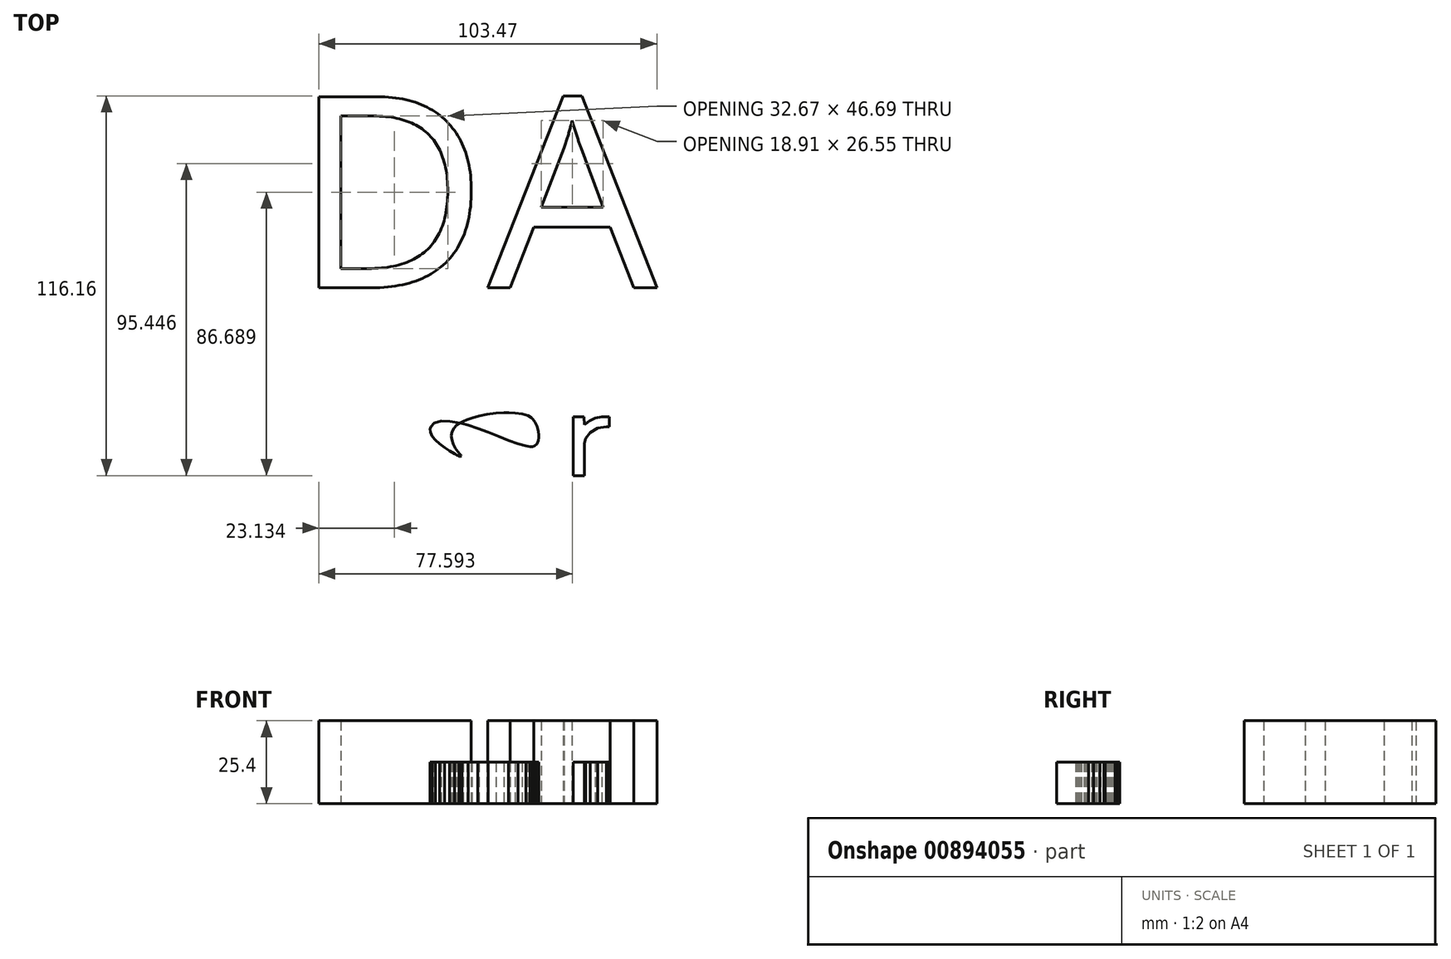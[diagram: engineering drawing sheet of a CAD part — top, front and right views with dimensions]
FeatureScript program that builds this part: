
annotation { "Feature Type Name" : "Feature", "Feature Type Description" : "" }
export const myFeature = defineFeature(function(context is Context, id is Id, definition is map)
    precondition{}
    {
        {
            var Q0;
            Q0=qCreatedBy(makeId("Top.planeOp"),FACE);
            var sketch = newSketch(context, id + "F0", { "sketchPlane" : qUnion([Q0])});
            skLineSegment(sketch, "E0", {"start": v(38.55, 8.55) * mm, "end": v(38.55, 11.6) * mm});
            skLineSegment(sketch, "E1", {"start": v(38.55, 11.6) * mm, "end": v(37.96, 11.65) * mm});
            skLineSegment(sketch, "E2", {"start": v(37.96, 11.65) * mm, "end": v(36.18, 11.62) * mm});
            skLineSegment(sketch, "E3", {"start": v(36.18, 11.62) * mm, "end": v(34.15, 11.22) * mm});
            skLineSegment(sketch, "E4", {"start": v(34.15, 11.22) * mm, "end": v(32.41, 10.4) * mm});
            skLineSegment(sketch, "E5", {"start": v(32.41, 10.4) * mm, "end": v(31.25, 9.5) * mm});
            skLineSegment(sketch, "E6", {"start": v(31.25, 9.5) * mm, "end": v(30.91, 9.15) * mm});
            skLineSegment(sketch, "E7", {"start": v(30.91, 9.15) * mm, "end": v(30.73, 11.63) * mm});
            skLineSegment(sketch, "E8", {"start": v(30.73, 11.63) * mm, "end": v(27.47, 11.63) * mm});
            skLineSegment(sketch, "E9", {"start": v(27.47, 11.63) * mm, "end": v(27.47, -6.37) * mm});
            skLineSegment(sketch, "E10", {"start": v(27.47, -6.37) * mm, "end": v(30.91, -6.37) * mm});
            skLineSegment(sketch, "E11", {"start": v(30.91, -6.37) * mm, "end": v(30.91, 2.96) * mm});
            skLineSegment(sketch, "E12", {"start": v(30.91, 2.96) * mm, "end": v(30.91, 3.46) * mm});
            skLineSegment(sketch, "E13", {"start": v(30.91, 3.46) * mm, "end": v(31.33, 4.97) * mm});
            skLineSegment(sketch, "E14", {"start": v(31.33, 4.97) * mm, "end": v(32.65, 6.85) * mm});
            skLineSegment(sketch, "E15", {"start": v(32.65, 6.85) * mm, "end": v(35.02, 8.17) * mm});
            skLineSegment(sketch, "E16", {"start": v(35.02, 8.17) * mm, "end": v(37.67, 8.6) * mm});
            skLineSegment(sketch, "E17", {"start": v(37.67, 8.6) * mm, "end": v(38.55, 8.55) * mm});
            skLineSegment(sketch, "E18", {"start": v(-7.86, 9.23) * mm, "end": v(-7.81, 9.26) * mm});
            skLineSegment(sketch, "E19", {"start": v(-7.81, 9.26) * mm, "end": v(-7.28, 9.6) * mm});
            skLineSegment(sketch, "E20", {"start": v(-7.28, 9.6) * mm, "end": v(-7.23, 9.62) * mm});
            skLineSegment(sketch, "E21", {"start": v(-7.23, 9.62) * mm, "end": v(-7.16, 9.66) * mm});
            skLineSegment(sketch, "E22", {"start": v(-7.16, 9.66) * mm, "end": v(-7.23, 9.67) * mm});
            skLineSegment(sketch, "E23", {"start": v(-7.23, 9.67) * mm, "end": v(-7.97, 9.87) * mm});
            skLineSegment(sketch, "E24", {"start": v(-7.97, 9.87) * mm, "end": v(-10.25, 10.27) * mm});
            skLineSegment(sketch, "E25", {"start": v(-10.25, 10.27) * mm, "end": v(-12.96, 10.31) * mm});
            skLineSegment(sketch, "E26", {"start": v(-12.96, 10.31) * mm, "end": v(-15.04, 9.66) * mm});
            skLineSegment(sketch, "E27", {"start": v(-15.04, 9.66) * mm, "end": v(-16.06, 8.6) * mm});
            skLineSegment(sketch, "E28", {"start": v(-16.06, 8.6) * mm, "end": v(-16.19, 8.19) * mm});
            skLineSegment(sketch, "E29", {"start": v(-16.19, 8.19) * mm, "end": v(-16.28, 7.9) * mm});
            skLineSegment(sketch, "E30", {"start": v(-16.28, 7.9) * mm, "end": v(-16.24, 6.94) * mm});
            skLineSegment(sketch, "E31", {"start": v(-16.24, 6.94) * mm, "end": v(-15.7, 5.7) * mm});
            skLineSegment(sketch, "E32", {"start": v(-15.7, 5.7) * mm, "end": v(-14.72, 4.47) * mm});
            skLineSegment(sketch, "E33", {"start": v(-14.72, 4.47) * mm, "end": v(-13.42, 3.3) * mm});
            skLineSegment(sketch, "E34", {"start": v(-13.42, 3.3) * mm, "end": v(-11.92, 2.21) * mm});
            skLineSegment(sketch, "E35", {"start": v(-11.92, 2.21) * mm, "end": v(-10.36, 1.22) * mm});
            skLineSegment(sketch, "E36", {"start": v(-10.36, 1.22) * mm, "end": v(-8.87, 0.35) * mm});
            skLineSegment(sketch, "E37", {"start": v(-8.87, 0.35) * mm, "end": v(-7.9, -0.19) * mm});
            skLineSegment(sketch, "E38", {"start": v(-7.9, -0.19) * mm, "end": v(-7.57, -0.37) * mm});
            skLineSegment(sketch, "E39", {"start": v(-7.57, -0.37) * mm, "end": v(-7.48, -0.42) * mm});
            skLineSegment(sketch, "E40", {"start": v(-7.48, -0.42) * mm, "end": v(-7.15, -0.53) * mm});
            skLineSegment(sketch, "E41", {"start": v(-7.15, -0.53) * mm, "end": v(-6.9, -0.5) * mm});
            skLineSegment(sketch, "E42", {"start": v(-6.9, -0.5) * mm, "end": v(-6.86, -0.33) * mm});
            skLineSegment(sketch, "E43", {"start": v(-6.86, -0.33) * mm, "end": v(-6.99, -0.08) * mm});
            skLineSegment(sketch, "E44", {"start": v(-6.99, -0.08) * mm, "end": v(-7.05, -0.02) * mm});
            skLineSegment(sketch, "E45", {"start": v(-7.05, -0.02) * mm, "end": v(-7.24, 0.21) * mm});
            skLineSegment(sketch, "E46", {"start": v(-7.24, 0.21) * mm, "end": v(-7.8, 0.92) * mm});
            skLineSegment(sketch, "E47", {"start": v(-7.8, 0.92) * mm, "end": v(-8.55, 2.01) * mm});
            skLineSegment(sketch, "E48", {"start": v(-8.55, 2.01) * mm, "end": v(-9.2, 3.21) * mm});
            skLineSegment(sketch, "E49", {"start": v(-9.2, 3.21) * mm, "end": v(-9.65, 4.48) * mm});
            skLineSegment(sketch, "E50", {"start": v(-9.65, 4.48) * mm, "end": v(-9.84, 5.76) * mm});
            skLineSegment(sketch, "E51", {"start": v(-9.84, 5.76) * mm, "end": v(-9.66, 7) * mm});
            skLineSegment(sketch, "E52", {"start": v(-9.66, 7) * mm, "end": v(-9.03, 8.18) * mm});
            skLineSegment(sketch, "E53", {"start": v(-9.03, 8.18) * mm, "end": v(-8.18, 9.02) * mm});
            skLineSegment(sketch, "E54", {"start": v(-8.18, 9.02) * mm, "end": v(-7.86, 9.23) * mm});
            skLineSegment(sketch, "E55", {"start": v(-7.17, 9.66) * mm, "end": v(-6.93, 9.8) * mm});
            skLineSegment(sketch, "E56", {"start": v(-6.93, 9.8) * mm, "end": v(-6.22, 10.17) * mm});
            skLineSegment(sketch, "E57", {"start": v(-6.22, 10.17) * mm, "end": v(-5.05, 10.69) * mm});
            skLineSegment(sketch, "E58", {"start": v(-5.05, 10.69) * mm, "end": v(-3.44, 11.28) * mm});
            skLineSegment(sketch, "E59", {"start": v(-3.44, 11.28) * mm, "end": v(-1.4, 11.88) * mm});
            skLineSegment(sketch, "E60", {"start": v(-1.4, 11.88) * mm, "end": v(1.05, 12.4) * mm});
            skLineSegment(sketch, "E61", {"start": v(1.05, 12.4) * mm, "end": v(3.9, 12.77) * mm});
            skLineSegment(sketch, "E62", {"start": v(3.9, 12.77) * mm, "end": v(6.33, 12.91) * mm});
            skLineSegment(sketch, "E63", {"start": v(6.33, 12.91) * mm, "end": v(7.14, 12.91) * mm});
            skLineSegment(sketch, "E64", {"start": v(7.14, 12.91) * mm, "end": v(7.77, 12.91) * mm});
            skLineSegment(sketch, "E65", {"start": v(7.77, 12.91) * mm, "end": v(9.67, 12.8) * mm});
            skLineSegment(sketch, "E66", {"start": v(9.67, 12.8) * mm, "end": v(11.88, 12.49) * mm});
            skLineSegment(sketch, "E67", {"start": v(11.88, 12.49) * mm, "end": v(13.67, 11.93) * mm});
            skLineSegment(sketch, "E68", {"start": v(13.67, 11.93) * mm, "end": v(14.66, 11.38) * mm});
            skLineSegment(sketch, "E69", {"start": v(14.66, 11.38) * mm, "end": v(14.92, 11.13) * mm});
            skLineSegment(sketch, "E70", {"start": v(14.92, 11.13) * mm, "end": v(15.17, 10.88) * mm});
            skLineSegment(sketch, "E71", {"start": v(15.17, 10.88) * mm, "end": v(15.8, 10) * mm});
            skLineSegment(sketch, "E72", {"start": v(15.8, 10) * mm, "end": v(16.44, 8.64) * mm});
            skLineSegment(sketch, "E73", {"start": v(16.44, 8.64) * mm, "end": v(16.83, 7.14) * mm});
            skLineSegment(sketch, "E74", {"start": v(16.83, 7.14) * mm, "end": v(16.96, 5.99) * mm});
            skLineSegment(sketch, "E75", {"start": v(16.96, 5.99) * mm, "end": v(16.96, 5.6) * mm});
            skLineSegment(sketch, "E76", {"start": v(16.96, 5.6) * mm, "end": v(16.96, 5.3) * mm});
            skLineSegment(sketch, "E77", {"start": v(16.96, 5.3) * mm, "end": v(16.83, 4.38) * mm});
            skLineSegment(sketch, "E78", {"start": v(16.83, 4.38) * mm, "end": v(16.42, 3.36) * mm});
            skLineSegment(sketch, "E79", {"start": v(16.42, 3.36) * mm, "end": v(15.72, 2.67) * mm});
            skLineSegment(sketch, "E80", {"start": v(15.72, 2.67) * mm, "end": v(14.99, 2.42) * mm});
            skLineSegment(sketch, "E81", {"start": v(14.99, 2.42) * mm, "end": v(14.74, 2.42) * mm});
            skLineSegment(sketch, "E82", {"start": v(14.74, 2.42) * mm, "end": v(14.3, 2.42) * mm});
            skLineSegment(sketch, "E83", {"start": v(14.3, 2.42) * mm, "end": v(12.95, 2.68) * mm});
            skLineSegment(sketch, "E84", {"start": v(12.95, 2.68) * mm, "end": v(10.55, 3.39) * mm});
            skLineSegment(sketch, "E85", {"start": v(10.55, 3.39) * mm, "end": v(7.72, 4.4) * mm});
            skLineSegment(sketch, "E86", {"start": v(7.72, 4.4) * mm, "end": v(4.62, 5.6) * mm});
            skLineSegment(sketch, "E87", {"start": v(4.62, 5.6) * mm, "end": v(1.41, 6.87) * mm});
            skLineSegment(sketch, "E88", {"start": v(1.41, 6.87) * mm, "end": v(-1.73, 8.05) * mm});
            skLineSegment(sketch, "E89", {"start": v(-1.73, 8.05) * mm, "end": v(-4.64, 9.02) * mm});
            skLineSegment(sketch, "E90", {"start": v(-4.64, 9.02) * mm, "end": v(-6.53, 9.54) * mm});
            skLineSegment(sketch, "E91", {"start": v(-6.53, 9.54) * mm, "end": v(-7.17, 9.66) * mm});
            skSolve(sketch);
        }
        {
            var Q0;
            {var subQ5=sQuery(id+"F0.wireOp",EDGE,"E56");Q0=makeQuery(id+"F0.imprint","IMPRINT",FACE,{"disambiguationData":[TD([[makeQuery(id+"F0.imprint","IMPRINT",EDGE,{"derivedFrom":subQ5}),-1.0]])]});}
            var Q1;
            Q1=makeQuery(id+"F0.imprint","IMPRINT",FACE,{"disambiguationData":[TD([[makeQuery(id+"F0.imprint","IMPRINT",EDGE,{"derivedFrom":sQuery(id+"F0.wireOp",EDGE,"1403de3f-786f-42e8-bdc0-92bf3ea4d2cf")}),-1.0]])]});
            var Q2;
            Q2=makeQuery(id+"F0.imprint","IMPRINT",FACE,{"disambiguationData":[TD([[makeQuery(id+"F0.imprint","IMPRINT",EDGE,{"derivedFrom":sQuery(id+"F0.wireOp",EDGE,"95009ed1-91f1-4808-89fd-04971f9fd36b")}),-1.0]])]});
            var Q3;
            Q3=makeQuery(id+"F0.imprint","IMPRINT",FACE,{"disambiguationData":[TD([[makeQuery(id+"F0.imprint","IMPRINT",EDGE,{"derivedFrom":sQuery(id+"F0.wireOp",EDGE,"E0")}),1.0]])]});
            var Q4;
            Q4=makeQuery(id+"F0.imprint","IMPRINT",FACE,{"disambiguationData":[TD([[makeQuery(id+"F0.imprint","IMPRINT",EDGE,{"derivedFrom":sQuery(id+"F0.wireOp",EDGE,"537d8619-0df1-4f76-a38b-5c3195fe6c56")}),1.0]])]});
            var Q5;
            Q5=makeQuery(id+"F0.imprint","IMPRINT",FACE,{"disambiguationData":[TD([[makeQuery(id+"F0.imprint","IMPRINT",EDGE,{"derivedFrom":sQuery(id+"F0.wireOp",EDGE,"53540bf8-cc36-49fe-be7e-849ee8bb7355")}),-1.0]])]});
            var Q6;
            Q6=makeQuery(id+"F0.imprint","IMPRINT",FACE,{"disambiguationData":[TD([[makeQuery(id+"F0.imprint","IMPRINT",EDGE,{"derivedFrom":sQuery(id+"F0.wireOp",EDGE,"5d299cd5-eb9d-4ea7-a19f-d956b55c55ad")}),-1.0]])]});
            var Q7;
            Q7=makeQuery(id+"F0.imprint","IMPRINT",FACE,{"disambiguationData":[TD([[makeQuery(id+"F0.imprint","IMPRINT",EDGE,{"derivedFrom":sQuery(id+"F0.wireOp",EDGE,"88f4a6f8-3216-4552-9583-ee77e8b5c767")}),-1.0]])]});
            var Q8;
            {var subQ0=sQuery(id+"F0.wireOp",EDGE,"499cde78-be49-40a4-880d-d042f24b3584");Q8=makeQuery(id+"F0.imprint","IMPRINT",FACE,{"disambiguationData":[TD([[makeQuery(id+"F0.imprint","IMPRINT",EDGE,{"derivedFrom":subQ0}),-1.0]])]});}
            var Q9;
            Q9=makeQuery(id+"F0.imprint","IMPRINT",FACE,{"disambiguationData":[TD([[makeQuery(id+"F0.imprint","IMPRINT",EDGE,{"derivedFrom":sQuery(id+"F0.wireOp",EDGE,"f5d51b6b-fd86-4680-a26f-6e4a6e33f496")}),-1.0]])]});
            var Q10;
            Q10=makeQuery(id+"F0.imprint","IMPRINT",FACE,{"disambiguationData":[TD([[makeQuery(id+"F0.imprint","IMPRINT",EDGE,{"derivedFrom":sQuery(id+"F0.wireOp",EDGE,"E18")}),1.0]])]});
            var Q11;
            Q11=makeQuery(id+"F0.imprint","IMPRINT",FACE,{"disambiguationData":[TD([[makeQuery(id+"F0.imprint","IMPRINT",EDGE,{"derivedFrom":sQuery(id+"F0.wireOp",EDGE,"d14cbd88-a913-48c0-9fde-35ce2438bb89")}),1.0]])]});
            var Q12;
            Q12=makeQuery(id+"F0.imprint","IMPRINT",FACE,{"disambiguationData":[TD([[makeQuery(id+"F0.imprint","IMPRINT",EDGE,{"derivedFrom":sQuery(id+"F0.wireOp",EDGE,"56bfb7e6-9a1f-421a-9683-003b9129566a")}),1.0]])]});
            var Q13;
            Q13=makeQuery(id+"F0.imprint","IMPRINT",FACE,{"disambiguationData":[TD([[makeQuery(id+"F0.imprint","IMPRINT",EDGE,{"derivedFrom":sQuery(id+"F0.wireOp",EDGE,"ad045c7c-f0ab-4b8a-855a-bf2486b68ccc")}),1.0]])]});
            var Q14;
            Q14=makeQuery(id+"F0.imprint","IMPRINT",FACE,{"disambiguationData":[TD([[makeQuery(id+"F0.imprint","IMPRINT",EDGE,{"derivedFrom":sQuery(id+"F0.wireOp",EDGE,"f15a1d2e-a023-4afb-ae37-dc3aa092487f")}),1.0]])]});
            var Q15;
            {var subQ0=sQuery(id+"F0.wireOp",EDGE,"907b8c1e-9dad-4756-b5b3-93d8dea9a1bf");var subQ1=sQuery(id+"F0.wireOp",EDGE,"2761c65c-d06f-425f-8b3a-7dbb7bd44bb6");var subQ2=makeQuery(id+"F0.imprint","INTERSECT",VERTEX,{"derivedFrom":[subQ1,subQ0]});Q15=makeQuery(id+"F0.imprint","IMPRINT",FACE,{"disambiguationData":[TD([[makeQuery(id+"F0.imprint","IMPRINT",EDGE,{"disambiguationData":[TD([[subQ2,1.0]])],"derivedFrom":subQ1}),1.0]])]});}
            var Q16;
            {var subQ0=sQuery(id+"F0.wireOp",EDGE,"E22");var subQ1=sQuery(id+"F0.wireOp",EDGE,"E21");var subQ2=makeQuery(id+"F0.imprint","INTERSECT",VERTEX,{"derivedFrom":[subQ1,subQ0]});Q16=makeQuery(id+"F0.imprint","IMPRINT",FACE,{"disambiguationData":[TD([[makeQuery(id+"F0.imprint","IMPRINT",EDGE,{"disambiguationData":[TD([[subQ2,1.0]])],"derivedFrom":subQ1}),1.0]])]});}
            var Q17;
            Q17=makeQuery(id+"F0.imprint","IMPRINT",FACE,{"disambiguationData":[TD([[makeQuery(id+"F0.imprint","IMPRINT",EDGE,{"derivedFrom":sQuery(id+"F0.wireOp",EDGE,"64ebe587-57e8-4b0d-80bb-392c409691db")}),1.0]])]});
            extrude(context, id + "F1", {"entities" : qUnion([Q0, Q1, Q2, Q3, Q4, Q5, Q6, Q7, Q8, Q9, Q10, Q11, Q12, Q13, Q14, Q15, Q16, Q17]), "depth" : 12.7 * mm, "offsetDistance" : 25.4 * mm});
        }
        {
            var Q0;
            Q0=qCreatedBy(makeId("Top.planeOp"),FACE);
            var sketch = newSketch(context, id + "F2", { "sketchPlane" : qUnion([Q0])});
            skText(sketch, "E92", { "text": "DA", "fontName": "OpenSans-Regular.ttf"});
            const initialGuessF2  = {"E92": [-0.0584, 0.0511, 1, 0, 0.05895]};
            skSetInitialGuess(sketch, initialGuessF2);
            skSolve(sketch);
        }
        {
            var Q0;
            Q0=qSketchRegion(id+"F2",true);
            extrude(context, id + "F3", {"entities" : qUnion([Q0]), "depth" : 25.4 * mm, "offsetDistance" : 25.4 * mm});
        }
    });
